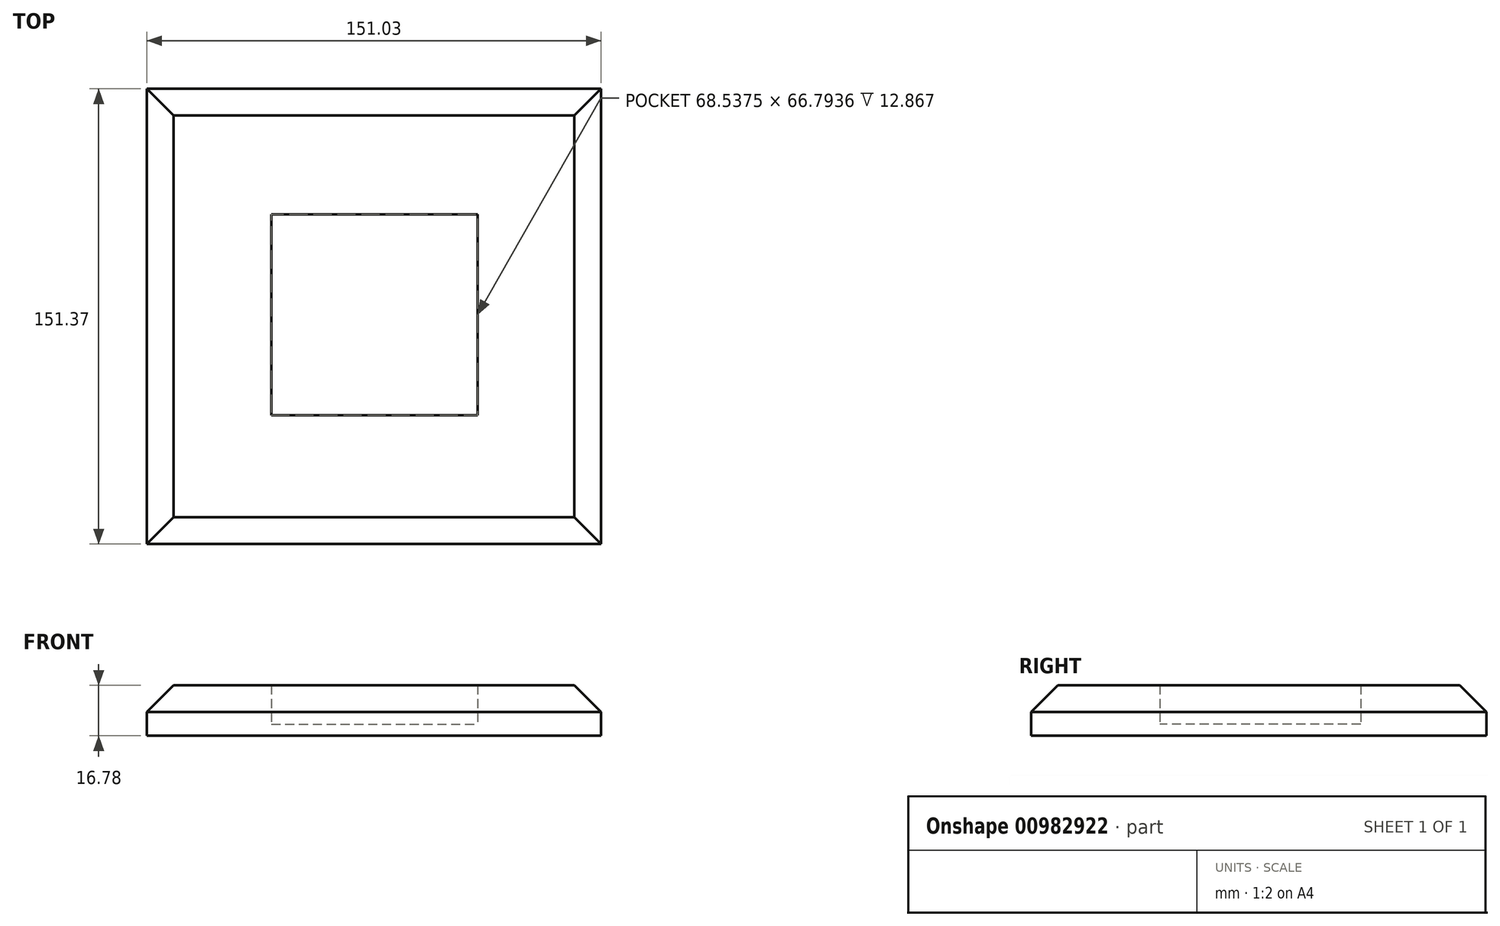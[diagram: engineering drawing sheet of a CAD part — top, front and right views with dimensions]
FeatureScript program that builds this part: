
annotation { "Feature Type Name" : "Feature", "Feature Type Description" : "" }
export const myFeature = defineFeature(function(context is Context, id is Id, definition is map)
    precondition{}
    {
        {
            var Q0;
            Q0=qCreatedBy(makeId("Top.planeOp"),FACE);
            var sketch = newSketch(context, id + "F0", { "sketchPlane" : qUnion([Q0])});
            skLineSegment(sketch, "E0.bottom", {"start": v(-75.47, 76.1) * mm, "end": v(75.56, 76.1) * mm});
            skLineSegment(sketch, "E0.top", {"start": v(-75.47, -75.27) * mm, "end": v(75.56, -75.27) * mm});
            skLineSegment(sketch, "E0.left", {"start": v(-75.47, 76.1) * mm, "end": v(-75.47, -75.27) * mm});
            skLineSegment(sketch, "E0.right", {"start": v(75.56, 76.1) * mm, "end": v(75.56, -75.27) * mm});
            skSolve(sketch);
        }
        {
            var Q0;
            Q0 = qSketchRegion(id + "F0", true);
            extrude(context, id + "F1", {"entities" : qUnion([Q0]), "depth" : 6.76 * mm, "offsetDistance" : 25.4 * mm});
        }
        {
            var Q0;
            Q0=makeQuery(id+"F1.opExtrude","CAP_FACE",FACE,{"disambiguationData":[OSD([sQuery(id+"F0.wireOp",EDGE,"E0.bottom"),sQuery(id+"F0.wireOp",EDGE,"E0.top"),sQuery(id+"F0.wireOp",EDGE,"E0.left"),sQuery(id+"F0.wireOp",EDGE,"E0.right")])],"isStart":false});
            var sketch = newSketch(context, id + "F2", { "sketchPlane" : qUnion([Q0])});
            skSolve(sketch);
        }
        {
            var Q0;
            Q0=makeQuery(id+"F2.imprint","IMPRINT",FACE,{"disambiguationData":[TD([[makeQuery(id+"F2.imprint","IMPRINT",EDGE,{"derivedFrom":makeQuery(id+"F1.opExtrude","CAP_EDGE",EDGE,{"disambiguationData":[OSD([sQuery(id+"F0.wireOp",EDGE,"E0.bottom")])],"isStart":false})}),-1.0]])]});
            extrude(context, id + "F3", {"entities" : qUnion([Q0]), "operationType" : NewBodyOperationType.ADD, "depth" : 10.02 * mm, "offsetDistance" : 25.4 * mm});
        }
        {
            var Q0;
            Q0=makeQuery(id+"F3.opExtrude","CAP_EDGE",EDGE,{"disambiguationData":[OSD([sQuery(id+"F0.wireOp",EDGE,"E0.top")])],"isStart":false});
            var Q1;
            Q1=makeQuery(id+"F3.opExtrude","CAP_EDGE",EDGE,{"disambiguationData":[OSD([sQuery(id+"F0.wireOp",EDGE,"E0.bottom")])],"isStart":false});
            var Q2;
            Q2=makeQuery(id+"F3.opExtrude","CAP_EDGE",EDGE,{"disambiguationData":[OSD([sQuery(id+"F0.wireOp",EDGE,"E0.right")])],"isStart":false});
            var Q3;
            Q3=makeQuery(id+"F3.opExtrude","CAP_EDGE",EDGE,{"disambiguationData":[OSD([sQuery(id+"F0.wireOp",EDGE,"E0.left")])],"isStart":false});
            chamfer(context, id + "F4", {"entities" : qUnion([Q0, Q1, Q2, Q3]), "width" : 8.9 * mm, "tangentPropagation" : true});
        }
        {
            var Q0;
            Q0=makeQuery(id+"F3.opExtrude","CAP_FACE",FACE,{"disambiguationData":[OSD([sQuery(id+"F0.wireOp",EDGE,"E0.bottom"),sQuery(id+"F0.wireOp",EDGE,"E0.top"),sQuery(id+"F0.wireOp",EDGE,"E0.left"),sQuery(id+"F0.wireOp",EDGE,"E0.right")])],"isStart":false});
            var sketch = newSketch(context, id + "F5", { "sketchPlane" : qUnion([Q0])});
            skLineSegment(sketch, "E1.bottom", {"start": v(-290.02, 67.2) * mm, "end": v(-152.95, 67.2) * mm});
            skLineSegment(sketch, "E1.top", {"start": v(-290.02, -66.38) * mm, "end": v(-152.95, -66.38) * mm});
            skLineSegment(sketch, "E1.left", {"start": v(-290.02, 67.2) * mm, "end": v(-290.02, -66.38) * mm});
            skLineSegment(sketch, "E1.right", {"start": v(-152.95, 67.2) * mm, "end": v(-152.95, -66.38) * mm});
            skSolve(sketch);
        }
        {
            var Q0;
            Q0=makeQuery(id+"F5.imprint","IMPRINT",FACE,{"disambiguationData":[TD([[makeQuery(id+"F5.imprint","IMPRINT",EDGE,{"derivedFrom":sQuery(id+"F5.wireOp",EDGE,"E1.bottom")}),-1.0]])]});
            var sketch = newSketch(context, id + "F6", { "sketchPlane" : qUnion([Q0])});
            skSolve(sketch);
        }
        {
            var Q0;
            Q0=makeQuery(id+"F6.imprint","IMPRINT",FACE,{"disambiguationData":[TD([[makeQuery(id+"F6.imprint","IMPRINT",EDGE,{"derivedFrom":makeQuery(id+"F5.imprint","IMPRINT",EDGE,{"derivedFrom":sQuery(id+"F5.wireOp",EDGE,"E1.bottom")})}),-1.0]])]});
            extrude(context, id + "F7", {"entities" : qUnion([Q0]), "depth" : 104.13 * mm, "offsetDistance" : 25.4 * mm});
        }
        {
            var Q0;
            Q0=makeQuery(id+"F7.opExtrude","SWEPT_BODY",BODY,{"disambiguationData":[OSD([sQuery(id+"F5.wireOp",EDGE,"E1.bottom"),sQuery(id+"F5.wireOp",EDGE,"E1.top"),sQuery(id+"F5.wireOp",EDGE,"E1.left"),sQuery(id+"F5.wireOp",EDGE,"E1.right")])]});
            transform(context, id + "F8", {"entities" : qUnion([Q0]), "transformType" : TransformType.TRANSLATION_3D, "dx" : 221.75 * mm, "dy" : 0.55 * mm, "dz" : -40.46 * mm, "makeCopy" : false});
        }
        {
            var Q0;
            Q0=makeQuery(id+"F7.opExtrude","SWEPT_BODY",BODY,{"disambiguationData":[OSD([sQuery(id+"F5.wireOp",EDGE,"E1.bottom"),sQuery(id+"F5.wireOp",EDGE,"E1.top"),sQuery(id+"F5.wireOp",EDGE,"E1.left"),sQuery(id+"F5.wireOp",EDGE,"E1.right")])]});
            var Q1;
            Q1=makeQuery(id+"F7.opExtrude","CAP_VERTEX",VERTEX,{"disambiguationData":[OSD([sQuery(id+"F5.wireOp",EDGE,"E1.top"),sQuery(id+"F5.wireOp",EDGE,"E1.right")])],"isStart":false});
            transform(context, id + "F9", {"entities" : qUnion([Q0]), "transformType" : TransformType.SCALE_UNIFORMLY, "scale" : .5, "scalePoint" : qUnion([Q1]), "makeCopy" : false});
        }
        {
            var Q0;
            Q0=makeQuery(id+"F7.opExtrude","SWEPT_BODY",BODY,{"disambiguationData":[OSD([sQuery(id+"F5.wireOp",EDGE,"E1.bottom"),sQuery(id+"F5.wireOp",EDGE,"E1.top"),sQuery(id+"F5.wireOp",EDGE,"E1.left"),sQuery(id+"F5.wireOp",EDGE,"E1.right")])]});
            transform(context, id + "F10", {"entities" : qUnion([Q0]), "transformType" : TransformType.TRANSLATION_3D, "dx" : -34.34 * mm, "dy" : 33.38 * mm, "dz" : -24.47 * mm, "makeCopy" : false});
        }
        {
            var Q0;
            Q0=makeQuery(id+"F7.opExtrude","SWEPT_BODY",BODY,{"disambiguationData":[OSD([sQuery(id+"F5.wireOp",EDGE,"E1.bottom"),sQuery(id+"F5.wireOp",EDGE,"E1.top"),sQuery(id+"F5.wireOp",EDGE,"E1.left"),sQuery(id+"F5.wireOp",EDGE,"E1.right")])]});
            var Q1;
            Q1=makeQuery(id+"F1.opExtrude","SWEPT_BODY",BODY,{"disambiguationData":[OSD([sQuery(id+"F0.wireOp",EDGE,"E0.bottom"),sQuery(id+"F0.wireOp",EDGE,"E0.top"),sQuery(id+"F0.wireOp",EDGE,"E0.left"),sQuery(id+"F0.wireOp",EDGE,"E0.right")])]});
            booleanBodies(context, id + "F11", {"operationType" : BooleanOperationType.SUBTRACTION, "tools" : qUnion([Q0]), "targets" : qUnion([Q1])});
        }
    });
